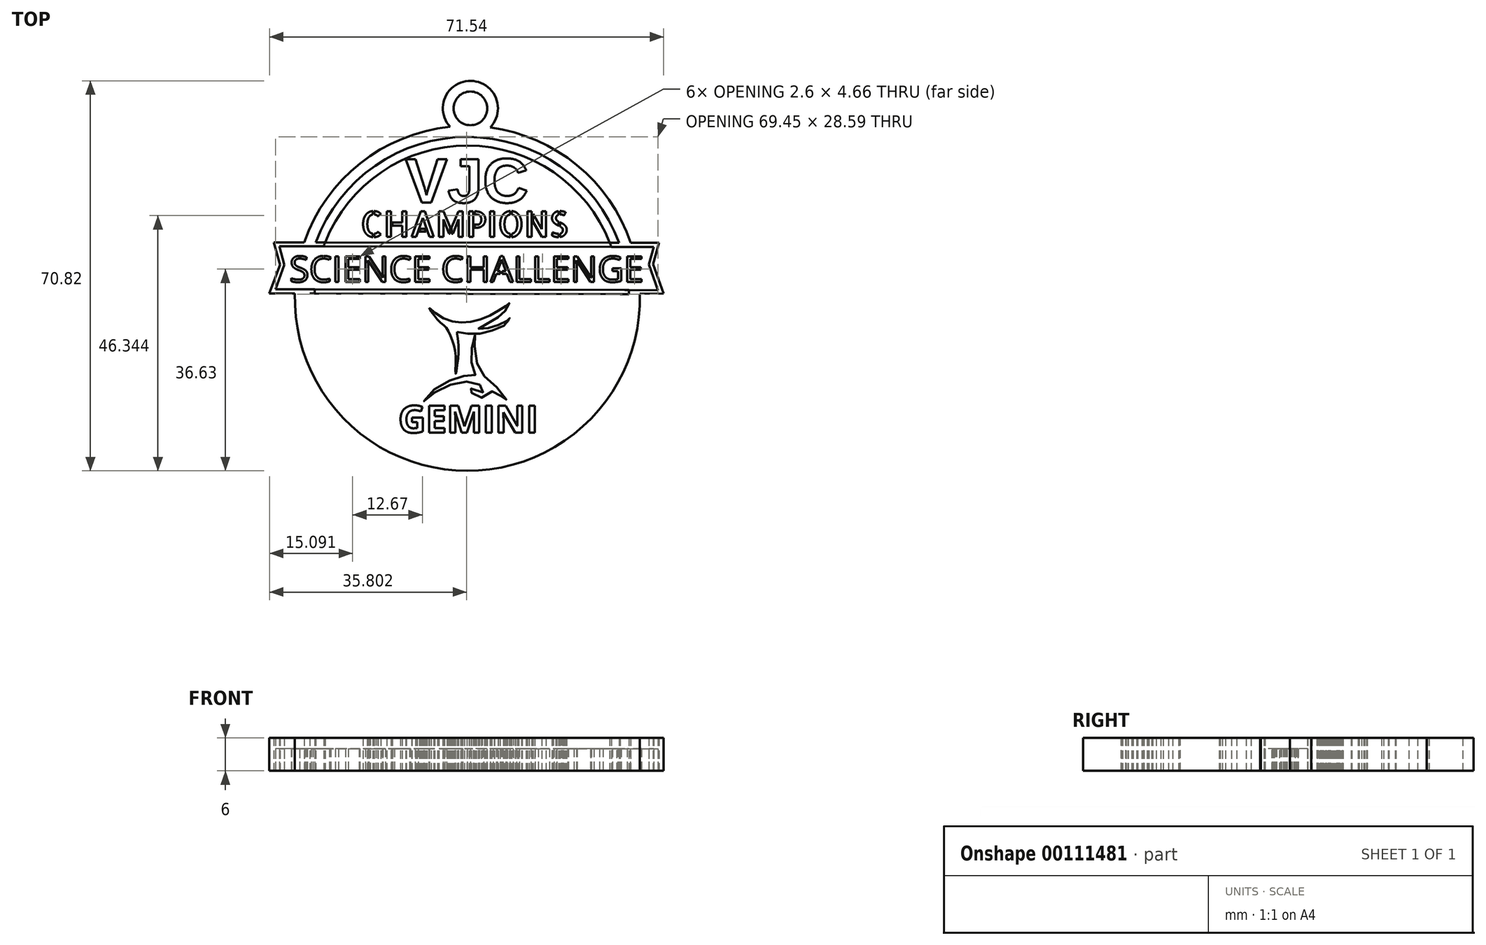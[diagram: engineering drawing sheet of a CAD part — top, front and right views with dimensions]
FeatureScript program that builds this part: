
annotation { "Feature Type Name" : "Feature", "Feature Type Description" : "" }
export const myFeature = defineFeature(function(context is Context, id is Id, definition is map)
    precondition{}
    {
        {
            var Q0;
            Q0=qCreatedBy(makeId("Top.planeOp"),FACE);
            var sketch = newSketch(context, id + "F0", { "sketchPlane" : qUnion([Q0])});
            skCircle(sketch, "E0", {"center": v(0.94, -3) * mm, "radius": 27.74 * mm});
            skPoint(sketch, "E0.first.point", {"position": v(1.58, 24.74) * mm});
            skPoint(sketch, "E0.second.point", {"position": v(0.52, -30.73) * mm});
            skPoint(sketch, "E0.third.point", {"position": v(-26.76, -1.33) * mm});
            skText(sketch, "E1", { "text": "CHAMPIONS", "fontName": "AllertaStencil-Regular.ttf"});
            skLineSegment(sketch, "E2", {"start": v(-24.87, 7.2) * mm, "end": v(-34.2, 7.2) * mm});
            skLineSegment(sketch, "E3", {"start": v(-34.2, 7.2) * mm, "end": v(-33.08, 3.11) * mm});
            skLineSegment(sketch, "E4", {"start": v(-33.08, 3.11) * mm, "end": v(-35, -2.1) * mm});
            skLineSegment(sketch, "E5", {"start": v(-35, -2.1) * mm, "end": v(-26.8, -2.1) * mm});
            skLineSegment(sketch, "E6", {"start": v(26.78, 7.1) * mm, "end": v(35.71, 7.1) * mm});
            skLineSegment(sketch, "E7", {"start": v(35.71, 7.1) * mm, "end": v(34.66, 3.21) * mm});
            skLineSegment(sketch, "E8", {"start": v(34.66, 3.21) * mm, "end": v(36.55, -2.1) * mm});
            skLineSegment(sketch, "E9", {"start": v(36.55, -2.1) * mm, "end": v(28.67, -2.25) * mm});
            skFitSpline(sketch, "E10", {"points": [v(-6, -4.72) * mm, v(-5.23, -5.35) * mm, v(-3.9, -6.35) * mm, v(-2.48, -6.98) * mm, v(-0.85, -7.35) * mm, v(0.35, -7.37) * mm, v(2.08, -7.15) * mm, v(3.86, -6.6) * mm, v(5.5, -5.84) * mm, v(6.83, -5.05) * mm, v(7.95, -4.34) * mm, v(8.2, -4.17) * mm, v(8.54, -3.89) * mm, v(8.14, -4.78) * mm, v(7.2, -5.82) * mm, v(5.2, -7.28) * mm, v(2.9, -8.45) * mm, v(3.98, -8.47) * mm, v(5.87, -8.12) * mm, v(7.76, -7.26) * mm, v(8.43, -6.75) * mm, v(8.6, -6.46) * mm, v(8.47, -7.15) * mm, v(6.46, -8.4) * mm, v(3.8, -9.28) * mm, v(1.11, -9.42) * mm, v(-0.95, -9.06) * mm], "startDerivative": vector(22.31, -18.25) * mm, "endDerivative": vector(-43, 9.84) * mm});
            skFitSpline(sketch, "E11", {"points": [v(-6, -4.72) * mm, v(-5.19, -6.01) * mm, v(-3.81, -7.48) * mm, v(-3.02, -8.2) * mm, v(-2.26, -9.47) * mm, v(-1.53, -11.45) * mm, v(-1.17, -13.95) * mm, v(-1.2, -16.67) * mm, v(-0.95, -15.45) * mm, v(-0.68, -11.98) * mm, v(-0.91, -9.36) * mm, v(-0.95, -9.06) * mm], "startDerivative": vector(8.3, -15) * mm, "endDerivative": vector(-0.86, 6) * mm});
            skFitSpline(sketch, "E12", {"points": [v(2.34, -9.66) * mm, v(2.02, -10.62) * mm, v(1.67, -12.76) * mm, v(1.67, -14.3) * mm, v(2.06, -16.19) * mm, v(2.36, -16.95) * mm, v(1.82, -16.92) * mm, v(-0.01, -17.17) * mm, v(-1.66, -17.64) * mm, v(-3.97, -18.79) * mm, v(-6.02, -20.44) * mm, v(-6.96, -21.68) * mm, v(-5.91, -20.77) * mm, v(-3.67, -19.33) * mm, v(-1.3, -18.4) * mm, v(0.83, -18.07) * mm, v(2.42, -18.3) * mm, v(3.7, -19.03) * mm, v(4.04, -19.68) * mm, v(3.45, -20.21) * mm, v(1.98, -19.81) * mm, v(1.3, -18.87) * mm, v(1.45, -19.8) * mm, v(2.36, -20.56) * mm, v(3.3, -21.02) * mm, v(4.84, -20.7) * mm, v(5.53, -19.8) * mm, v(6.38, -20.28) * mm, v(7.16, -20.84) * mm, v(8.14, -21.87) * mm, v(7.64, -20.68) * mm, v(6.28, -19.14) * mm, v(4.5, -17.53) * mm, v(3.33, -16.29) * mm, v(2.56, -14.18) * mm, v(2.24, -11.68) * mm, v(2.33, -10.24) * mm, v(2.34, -9.66) * mm]});
            skLineSegment(sketch, "E13", {"start": v(-24.87, 7.2) * mm, "end": v(28.1, 7.1) * mm});
            skLineSegment(sketch, "E14", {"start": v(-27.68, -2.1) * mm, "end": v(29.48, -2.24) * mm});
            skCircle(sketch, "E15.0", {"center": v(0.94, -3) * mm, "radius": 29.33 * mm});
            skCircle(sketch, "E16.0", {"center": v(0.94, -3) * mm, "radius": 31.31 * mm});
            skLineSegment(sketch, "E17.0", {"start": v(-24.87, 6.45) * mm, "end": v(28.1, 6.35) * mm});
            skLineSegment(sketch, "E18.0", {"start": v(-24.87, 6.45) * mm, "end": v(-33.21, 6.45) * mm});
            skLineSegment(sketch, "E19", {"start": v(28.1, 6.35) * mm, "end": v(34.73, 6.35) * mm});
            skLineSegment(sketch, "E20.0", {"start": v(-27.68, -1.35) * mm, "end": v(29.48, -1.49) * mm});
            skLineSegment(sketch, "E21", {"start": v(-27.68, -1.35) * mm, "end": v(-33.91, -1.33) * mm});
            skLineSegment(sketch, "E22", {"start": v(29.48, -1.49) * mm, "end": v(35.54, -1.5) * mm});
            skLineSegment(sketch, "E23.0", {"start": v(34.73, 6.35) * mm, "end": v(33.88, 3.18) * mm});
            skLineSegment(sketch, "E24.0", {"start": v(33.88, 3.18) * mm, "end": v(35.54, -1.5) * mm});
            skLineSegment(sketch, "E25.0", {"start": v(-32.3, 3.08) * mm, "end": v(-33.91, -1.33) * mm});
            skLineSegment(sketch, "E26.trimOffspring", {"start": v(-33.21, 6.45) * mm, "end": v(-32.3, 3.08) * mm});
            skText(sketch, "E27", { "text": "SCIENCE CHALLENGE", "fontName": "OpenSans-Regular.ttf"});
            skText(sketch, "E28", { "text": "GEMINI", "fontName": "OpenSans-Bold.ttf"});
            skText(sketch, "E29", { "text": "VJC", "fontName": "Arimo-Bold.ttf"});
            skLineSegment(sketch, "E30", {"start": v(6.9, 1.33) * mm, "end": v(6.9, 2.22) * mm});
            skLineSegment(sketch, "E31", {"start": v(6.9, 2.22) * mm, "end": v(7.18, 2.22) * mm});
            skLineSegment(sketch, "E32", {"start": v(7.18, 2.22) * mm, "end": v(7.26, 2.22) * mm});
            skLineSegment(sketch, "E33", {"start": v(7.26, 2.22) * mm, "end": v(7.26, 1.34) * mm});
            skLineSegment(sketch, "E34", {"start": v(7.26, 1.34) * mm, "end": v(6.9, 1.33) * mm});
            skCircle(sketch, "E35", {"center": v(1.48, 31.52) * mm, "radius": 3.06 * mm});
            skCircle(sketch, "E36.0", {"center": v(1.48, 31.52) * mm, "radius": 5 * mm});
            const initialGuessF0  = {"E1": [-0.01849, 0.00816, 1, 0, 0.00464], "E27": [-0.03136, 0, 1, 0, 0.0047], "E28": [-0.0116, -0.02738, 1, 0, 0.00494], "E29": [-0.01032, 0.01442, 1, 0, 0.00826]};
            skSetInitialGuess(sketch, initialGuessF0);
            skSolve(sketch);
        }
        {
            var Q0;
            Q0=makeQuery(id+"F0.imprint","IMPRINT",FACE,{"disambiguationData":[TD([[makeQuery(id+"F0.imprint","IMPRINT",EDGE,{"derivedFrom":sQuery(id+"F0.wireOp",EDGE,"E1.sketch_text.stroke-0")}),1.0]])]});
            var Q1;
            {var subQ0=sQuery(id+"F0.wireOp",EDGE,"E16.0");var subQ1=sQuery(id+"F0.wireOp",EDGE,"E2");var subQ2=makeQuery(id+"F0.imprint","INTERSECT",VERTEX,{"derivedFrom":[subQ1,subQ0]});Q1=makeQuery(id+"F0.imprint","IMPRINT",FACE,{"disambiguationData":[TD([[makeQuery(id+"F0.imprint","IMPRINT",EDGE,{"disambiguationData":[TD([[subQ2,1.0]])],"derivedFrom":subQ1}),-1.0]])]});}
            var Q2;
            Q2=makeQuery(id+"F0.imprint","IMPRINT",FACE,{"disambiguationData":[TD([[makeQuery(id+"F0.imprint","IMPRINT",EDGE,{"derivedFrom":sQuery(id+"F0.wireOp",EDGE,"26462852-2f77-49b2-9a3d-6dfd93b606f1.sketch_text.stroke-0")}),1.0]])]});
            var Q3;
            {var subQ0=sQuery(id+"F0.wireOp",EDGE,"E16.0");var subQ1=sQuery(id+"F0.wireOp",EDGE,"E5");var subQ2=makeQuery(id+"F0.imprint","INTERSECT",VERTEX,{"derivedFrom":[subQ1,subQ0]});Q3=makeQuery(id+"F0.imprint","IMPRINT",FACE,{"disambiguationData":[TD([[makeQuery(id+"F0.imprint","IMPRINT",EDGE,{"disambiguationData":[TD([[subQ2,-1.0]])],"derivedFrom":subQ1}),-1.0]])]});}
            var Q4;
            {var subQ7=sQuery(id+"F0.wireOp",EDGE,"E3");Q4=makeQuery(id+"F0.imprint","IMPRINT",FACE,{"disambiguationData":[TD([[makeQuery(id+"F0.imprint","IMPRINT",EDGE,{"derivedFrom":subQ7}),1.0]])]});}
            var Q5;
            {var subQ3=sQuery(id+"F0.wireOp",EDGE,"E18.0");var subQ10=makeQuery(id+"F0.imprint","IMPRINT",VERTEX,{"derivedFrom":subQ3});Q5=makeQuery(id+"F0.imprint","IMPRINT",FACE,{"disambiguationData":[TD([[makeQuery(id+"F0.imprint","IMPRINT",EDGE,{"disambiguationData":[TD([[subQ10,1.0]])],"derivedFrom":subQ3}),-1.0]])]});}
            var Q6;
            {var subQ0=sQuery(id+"F0.wireOp",EDGE,"E2");var subQ5=sQuery(id+"F0.wireOp",EDGE,"E15.0");var subQ6=makeQuery(id+"F0.imprint","INTERSECT",VERTEX,{"derivedFrom":[subQ0,subQ5]});Q6=makeQuery(id+"F0.imprint","IMPRINT",FACE,{"disambiguationData":[TD([[makeQuery(id+"F0.imprint","IMPRINT",EDGE,{"disambiguationData":[TD([[subQ6,-1.0]])],"derivedFrom":subQ5}),1.0]])]});}
            var Q7;
            {var subQ1=sQuery(id+"F0.wireOp",EDGE,"E6");var subQ6=sQuery(id+"F0.wireOp",EDGE,"E0");var subQ7=makeQuery(id+"F0.imprint","INTERSECT",VERTEX,{"derivedFrom":[subQ6,subQ1]});Q7=makeQuery(id+"F0.imprint","IMPRINT",FACE,{"disambiguationData":[TD([[makeQuery(id+"F0.imprint","IMPRINT",EDGE,{"disambiguationData":[TD([[subQ7,1.0]])],"derivedFrom":subQ6}),-1.0]])]});}
            var Q8;
            {var subQ0=sQuery(id+"F0.wireOp",EDGE,"E16.0");var subQ1=sQuery(id+"F0.wireOp",EDGE,"E6");var subQ2=makeQuery(id+"F0.imprint","INTERSECT",VERTEX,{"derivedFrom":[subQ1,subQ0]});Q8=makeQuery(id+"F0.imprint","IMPRINT",FACE,{"disambiguationData":[TD([[makeQuery(id+"F0.imprint","IMPRINT",EDGE,{"disambiguationData":[TD([[subQ2,1.0]])],"derivedFrom":subQ1}),-1.0]])]});}
            var Q9;
            {var subQ11=sQuery(id+"F0.wireOp",EDGE,"E7");Q9=makeQuery(id+"F0.imprint","IMPRINT",FACE,{"disambiguationData":[TD([[makeQuery(id+"F0.imprint","IMPRINT",EDGE,{"derivedFrom":subQ11}),-1.0]])]});}
            var Q10;
            {var subQ0=sQuery(id+"F0.wireOp",EDGE,"E14");var subQ1=sQuery(id+"F0.wireOp",EDGE,"E0");var subQ2=makeQuery(id+"F0.imprint","INTERSECT",VERTEX,{"disambiguationData":[OD(0.0)],"derivedFrom":[subQ1,subQ0]});Q10=makeQuery(id+"F0.imprint","IMPRINT",FACE,{"disambiguationData":[TD([[makeQuery(id+"F0.imprint","IMPRINT",EDGE,{"disambiguationData":[TD([[subQ2,-1.0]])],"derivedFrom":subQ1}),1.0]])]});}
            var Q11;
            {var subQ0=sQuery(id+"F0.wireOp",EDGE,"E14");var subQ3=sQuery(id+"F0.wireOp",EDGE,"E0");var subQ4=makeQuery(id+"F0.imprint","INTERSECT",VERTEX,{"disambiguationData":[OD(0.0)],"derivedFrom":[subQ3,subQ0]});Q11=makeQuery(id+"F0.imprint","IMPRINT",FACE,{"disambiguationData":[TD([[makeQuery(id+"F0.imprint","IMPRINT",EDGE,{"disambiguationData":[TD([[subQ4,-1.0]])],"derivedFrom":subQ3}),-1.0]])]});}
            var Q12;
            {var subQ0=sQuery(id+"F0.wireOp",EDGE,"E16.0");var subQ1=sQuery(id+"F0.wireOp",EDGE,"E9");var subQ2=makeQuery(id+"F0.imprint","INTERSECT",VERTEX,{"derivedFrom":[subQ1,subQ0]});Q12=makeQuery(id+"F0.imprint","IMPRINT",FACE,{"disambiguationData":[TD([[makeQuery(id+"F0.imprint","IMPRINT",EDGE,{"disambiguationData":[TD([[subQ2,-1.0]])],"derivedFrom":subQ1}),-1.0]])]});}
            var Q13;
            {var subQ0=sQuery(id+"F0.wireOp",EDGE,"E16.0");var subQ1=sQuery(id+"F0.wireOp",EDGE,"E2");var subQ2=makeQuery(id+"F0.imprint","INTERSECT",VERTEX,{"derivedFrom":[subQ1,subQ0]});Q13=makeQuery(id+"F0.imprint","IMPRINT",FACE,{"disambiguationData":[TD([[makeQuery(id+"F0.imprint","IMPRINT",EDGE,{"disambiguationData":[TD([[subQ2,1.0]])],"derivedFrom":subQ1}),1.0]])]});}
            var Q14;
            {var subQ0=sQuery(id+"F0.wireOp",EDGE,"E16.0");var subQ1=sQuery(id+"F0.wireOp",EDGE,"E5");var subQ2=makeQuery(id+"F0.imprint","INTERSECT",VERTEX,{"derivedFrom":[subQ1,subQ0]});Q14=makeQuery(id+"F0.imprint","IMPRINT",FACE,{"disambiguationData":[TD([[makeQuery(id+"F0.imprint","IMPRINT",EDGE,{"disambiguationData":[TD([[subQ2,-1.0]])],"derivedFrom":subQ1}),1.0]])]});}
            var Q15;
            {var subQ0=sQuery(id+"F0.wireOp",EDGE,"E5");var subQ1=sQuery(id+"F0.wireOp",EDGE,"E0");var subQ2=makeQuery(id+"F0.imprint","INTERSECT",VERTEX,{"derivedFrom":[subQ1,subQ0]});Q15=makeQuery(id+"F0.imprint","IMPRINT",FACE,{"disambiguationData":[TD([[makeQuery(id+"F0.imprint","IMPRINT",EDGE,{"disambiguationData":[TD([[subQ2,1.0]])],"derivedFrom":subQ1}),-1.0]])]});}
            var Q16;
            Q16=makeQuery(id+"F0.imprint","IMPRINT",FACE,{"disambiguationData":[TD([[makeQuery(id+"F0.imprint","IMPRINT",EDGE,{"derivedFrom":sQuery(id+"F0.wireOp",EDGE,"E10")}),1.0]])]});
            var Q17;
            {var subQ0=sQuery(id+"F0.wireOp",EDGE,"E36.0");var subQ1=sQuery(id+"F0.wireOp",EDGE,"E16.0");var subQ2=makeQuery(id+"F0.imprint","INTERSECT",VERTEX,{"disambiguationData":[OD(0.0)],"derivedFrom":[subQ1,subQ0]});Q17=makeQuery(id+"F0.imprint","IMPRINT",FACE,{"disambiguationData":[TD([[makeQuery(id+"F0.imprint","IMPRINT",EDGE,{"disambiguationData":[TD([[subQ2,-1.0]])],"derivedFrom":subQ1}),-1.0]])]});}
            var Q18;
            {var subQ0=sQuery(id+"F0.wireOp",EDGE,"E36.0");var subQ1=sQuery(id+"F0.wireOp",EDGE,"E16.0");var subQ2=makeQuery(id+"F0.imprint","INTERSECT",VERTEX,{"disambiguationData":[OD(0.0)],"derivedFrom":[subQ1,subQ0]});Q18=makeQuery(id+"F0.imprint","IMPRINT",FACE,{"disambiguationData":[TD([[makeQuery(id+"F0.imprint","IMPRINT",EDGE,{"disambiguationData":[TD([[subQ2,-1.0]])],"derivedFrom":subQ1}),1.0]])]});}
            extrude(context, id + "F1", {"entities" : qUnion([Q0, Q1, Q2, Q3, Q4, Q5, Q6, Q7, Q8, Q9, Q10, Q11, Q12, Q13, Q14, Q15, Q16, Q17, Q18]), "depth" : 6 * mm});
        }
        {
            var Q0;
            {var subQ0=sQuery(id+"F0.wireOp",EDGE,"E25.0");Q0=makeQuery(id+"F0.imprint","IMPRINT",FACE,{"disambiguationData":[TD([[makeQuery(id+"F0.imprint","IMPRINT",EDGE,{"derivedFrom":subQ0}),1.0]])]});}
            var Q1;
            {var subQ11=sQuery(id+"F0.wireOp",EDGE,"E27.sketch_text.stroke-16");Q1=makeQuery(id+"F0.imprint","IMPRINT",FACE,{"disambiguationData":[TD([[makeQuery(id+"F0.imprint","IMPRINT",EDGE,{"derivedFrom":subQ11}),1.0]])]});}
            var Q2;
            {var subQ0=sQuery(id+"F0.wireOp",EDGE,"E27.sketch_text.stroke-33");Q2=makeQuery(id+"F0.imprint","IMPRINT",FACE,{"disambiguationData":[TD([[makeQuery(id+"F0.imprint","IMPRINT",EDGE,{"derivedFrom":subQ0}),1.0]])]});}
            var Q3;
            {var subQ10=sQuery(id+"F0.wireOp",EDGE,"E27.sketch_text.stroke-28");Q3=makeQuery(id+"F0.imprint","IMPRINT",FACE,{"disambiguationData":[TD([[makeQuery(id+"F0.imprint","IMPRINT",EDGE,{"derivedFrom":subQ10}),1.0]])]});}
            var Q4;
            {var subQ25=sQuery(id+"F0.wireOp",EDGE,"E27.sketch_text.stroke-178");Q4=makeQuery(id+"F0.imprint","IMPRINT",FACE,{"disambiguationData":[TD([[makeQuery(id+"F0.imprint","IMPRINT",EDGE,{"derivedFrom":subQ25}),1.0]])]});}
            var Q5;
            {var subQ1=sQuery(id+"F0.wireOp",EDGE,"E27.sketch_text.stroke-198");var subQ3=sQuery(id+"F0.wireOp",EDGE,"E15.0");var subQ4=makeQuery(id+"F0.imprint","INTERSECT",VERTEX,{"derivedFrom":[subQ3,subQ1]});Q5=makeQuery(id+"F0.imprint","IMPRINT",FACE,{"disambiguationData":[TD([[makeQuery(id+"F0.imprint","IMPRINT",EDGE,{"disambiguationData":[TD([[subQ4,-1.0]])],"derivedFrom":subQ3}),-1.0]])]});}
            var Q6;
            {var subQ8=sQuery(id+"F0.wireOp",EDGE,"E23.0");Q6=makeQuery(id+"F0.imprint","IMPRINT",FACE,{"disambiguationData":[TD([[makeQuery(id+"F0.imprint","IMPRINT",EDGE,{"derivedFrom":subQ8}),-1.0]])]});}
            var Q7;
            {var subQ0=sQuery(id+"F0.wireOp",EDGE,"E27.sketch_text.stroke-6");Q7=makeQuery(id+"F0.imprint","IMPRINT",FACE,{"disambiguationData":[TD([[makeQuery(id+"F0.imprint","IMPRINT",EDGE,{"derivedFrom":subQ0}),1.0]])]});}
            var Q8;
            {var subQ6=sQuery(id+"F0.wireOp",EDGE,"E27.sketch_text.stroke-1");Q8=makeQuery(id+"F0.imprint","IMPRINT",FACE,{"disambiguationData":[TD([[makeQuery(id+"F0.imprint","IMPRINT",EDGE,{"derivedFrom":subQ6}),1.0]])]});}
            var Q9;
            {var subQ6=sQuery(id+"F0.wireOp",EDGE,"E27.sketch_text.stroke-189");Q9=makeQuery(id+"F0.imprint","IMPRINT",FACE,{"disambiguationData":[TD([[makeQuery(id+"F0.imprint","IMPRINT",EDGE,{"derivedFrom":subQ6}),1.0]])]});}
            var Q10;
            {var subQ5=sQuery(id+"F0.wireOp",EDGE,"E27.sketch_text.stroke-202");Q10=makeQuery(id+"F0.imprint","IMPRINT",FACE,{"disambiguationData":[TD([[makeQuery(id+"F0.imprint","IMPRINT",EDGE,{"derivedFrom":subQ5}),1.0]])]});}
            var Q11;
            {var subQ5=sQuery(id+"F0.wireOp",EDGE,"E27.sketch_text.stroke-206");Q11=makeQuery(id+"F0.imprint","IMPRINT",FACE,{"disambiguationData":[TD([[makeQuery(id+"F0.imprint","IMPRINT",EDGE,{"derivedFrom":subQ5}),1.0]])]});}
            var Q12;
            {var subQ0=sQuery(id+"F0.wireOp",EDGE,"E22");var subQ1=sQuery(id+"F0.wireOp",EDGE,"E15.0");var subQ2=makeQuery(id+"F0.imprint","INTERSECT",VERTEX,{"derivedFrom":[subQ1,subQ0]});Q12=makeQuery(id+"F0.imprint","IMPRINT",FACE,{"disambiguationData":[TD([[makeQuery(id+"F0.imprint","IMPRINT",EDGE,{"disambiguationData":[TD([[subQ2,-1.0]])],"derivedFrom":subQ1}),-1.0]])]});}
            var Q13;
            Q13=makeQuery(id+"F0.imprint","IMPRINT",FACE,{"disambiguationData":[TD([[makeQuery(id+"F0.imprint","IMPRINT",EDGE,{"derivedFrom":sQuery(id+"F0.wireOp",EDGE,"E27.sketch_text.stroke-133")}),1.0]])]});
            var Q14;
            {var subQ5=sQuery(id+"F0.wireOp",EDGE,"E27.sketch_text.stroke-26");Q14=makeQuery(id+"F0.imprint","IMPRINT",FACE,{"disambiguationData":[TD([[makeQuery(id+"F0.imprint","IMPRINT",EDGE,{"derivedFrom":subQ5}),1.0]])]});}
            var Q15;
            {var subQ1=sQuery(id+"F0.wireOp",EDGE,"E27.sketch_text.stroke-19");Q15=makeQuery(id+"F0.imprint","IMPRINT",FACE,{"disambiguationData":[TD([[makeQuery(id+"F0.imprint","IMPRINT",EDGE,{"derivedFrom":subQ1}),1.0]])]});}
            var Q16;
            {var subQ5=sQuery(id+"F0.wireOp",EDGE,"E34");Q16=makeQuery(id+"F0.imprint","IMPRINT",FACE,{"disambiguationData":[TD([[makeQuery(id+"F0.imprint","IMPRINT",EDGE,{"derivedFrom":subQ5}),-1.0]])]});}
            var Q17;
            {var subQ0=sQuery(id+"F0.wireOp",EDGE,"E33");var subQ1=sQuery(id+"F0.wireOp",EDGE,"E27.sketch_text.stroke-126");var subQ2=makeQuery(id+"F0.imprint","INTERSECT",VERTEX,{"derivedFrom":[subQ1,subQ0]});Q17=makeQuery(id+"F0.imprint","IMPRINT",FACE,{"disambiguationData":[TD([[makeQuery(id+"F0.imprint","IMPRINT",EDGE,{"disambiguationData":[TD([[subQ2,-1.0]])],"derivedFrom":subQ1}),-1.0]])]});}
            var Q18;
            {var subQ1=sQuery(id+"F0.wireOp",EDGE,"E31");Q18=makeQuery(id+"F0.imprint","IMPRINT",FACE,{"disambiguationData":[TD([[makeQuery(id+"F0.imprint","IMPRINT",EDGE,{"derivedFrom":subQ1}),-1.0]])]});}
            extrude(context, id + "F2", {"entities" : qUnion([Q0, Q1, Q2, Q3, Q4, Q5, Q6, Q7, Q8, Q9, Q10, Q11, Q12, Q13, Q14, Q15, Q16, Q17, Q18]), "depth" : 4 * mm});
        }
    });
